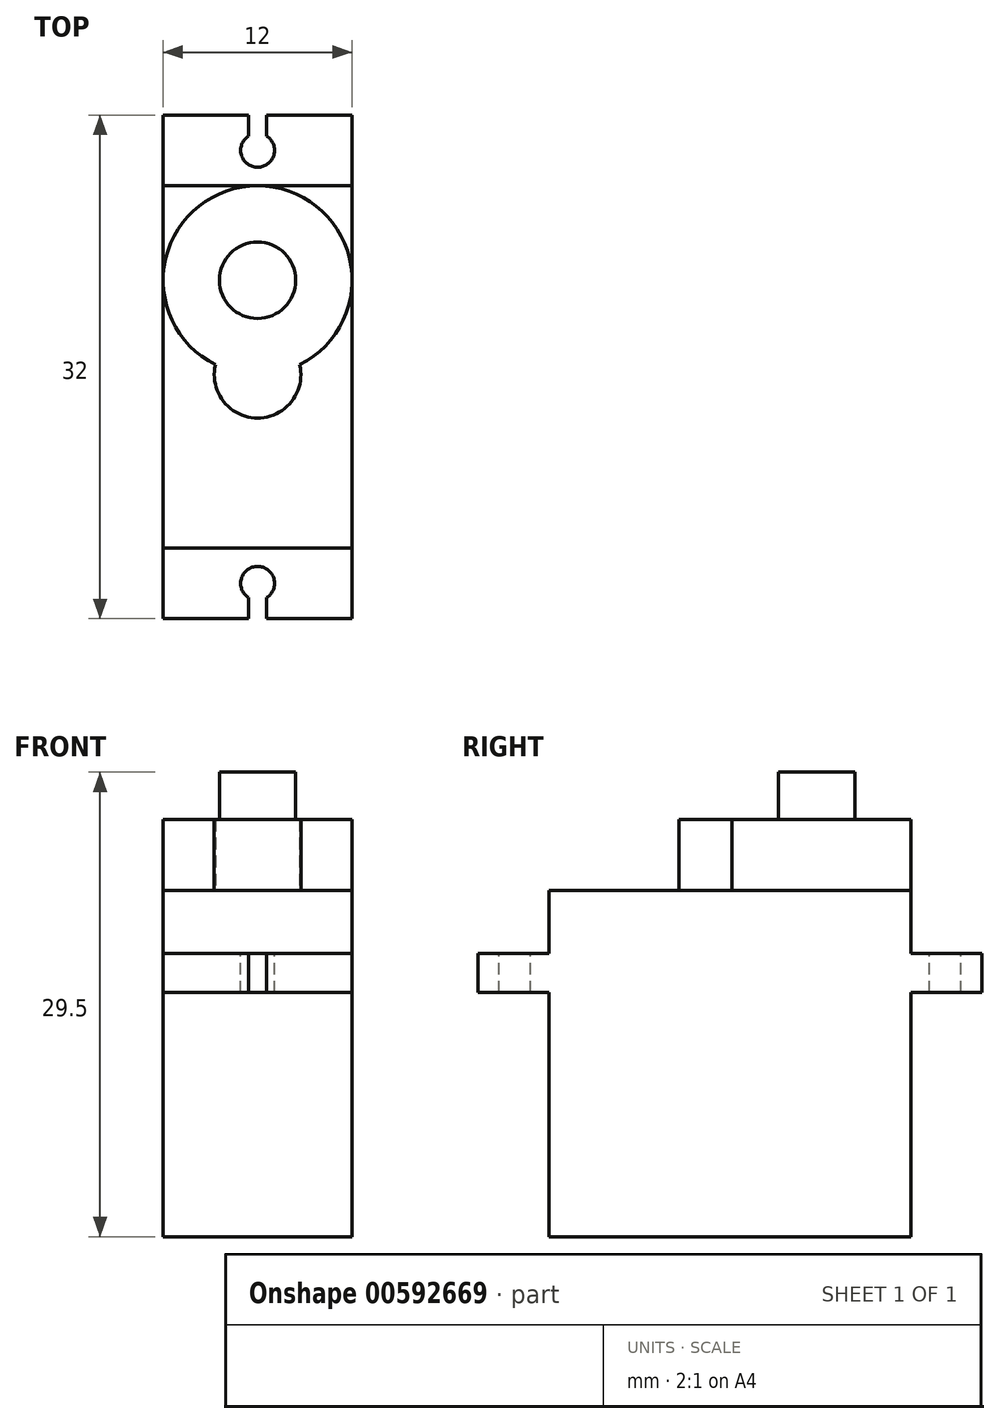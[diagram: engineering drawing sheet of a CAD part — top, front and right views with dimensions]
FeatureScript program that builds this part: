
annotation { "Feature Type Name" : "Feature", "Feature Type Description" : "" }
export const myFeature = defineFeature(function(context is Context, id is Id, definition is map)
    precondition{}
    {
        {
            var Q0;
            Q0=qCreatedBy(makeId("Top.planeOp"),FACE);
            var sketch = newSketch(context, id + "F0", { "sketchPlane" : qUnion([Q0])});
            skLineSegment(sketch, "E0.bottom", {"start": v(0, 0) * mm, "end": v(12, 0) * mm});
            skLineSegment(sketch, "E0.top", {"start": v(0, 23) * mm, "end": v(12, 23) * mm});
            skLineSegment(sketch, "E0.left", {"start": v(0, 0) * mm, "end": v(0, 23) * mm});
            skLineSegment(sketch, "E0.right", {"start": v(12, 0) * mm, "end": v(12, 23) * mm});
            skSolve(sketch);
        }
        {
            var Q0;
            Q0 = qSketchRegion(id + "F0", true);
            extrude(context, id + "F1", {"entities" : qUnion([Q0]), "depth" : 22 * mm, "offsetDistance" : 25 * mm});
        }
        {
            var Q0;
            Q0=qCreatedBy(makeId("Top.planeOp"),FACE);
            cPlane(context, id + "F2", {"entities" : qUnion([Q0]), "cplaneType" : CPlaneType.OFFSET, "offset" : 15.5 * mm, "width" : 150 * mm, "height" : 150 * mm});
        }
        {
            var Q0;
            Q0=qCreatedBy(id+"F2.planeOp",FACE);
            var sketch = newSketch(context, id + "F3", { "sketchPlane" : qUnion([Q0])});
            skLineSegment(sketch, "E1.0", {"start": v(0, 23) * mm, "end": v(12, 23) * mm});
            skPoint(sketch, "E2.0", {"position": v(0, 11.5) * mm});
            skPoint(sketch, "E3.0", {"position": v(12, 11.5) * mm});
            skLineSegment(sketch, "E4", {"start": v(0, 11.5) * mm, "end": v(12, 11.5) * mm, "construction": true});
            skLineSegment(sketch, "E5", {"start": v(0, 23) * mm, "end": v(0, 27.5) * mm});
            skLineSegment(sketch, "E6", {"start": v(0, 27.5) * mm, "end": v(12, 27.5) * mm});
            skLineSegment(sketch, "E7", {"start": v(12, 27.5) * mm, "end": v(12, 23) * mm});
            skLineSegment(sketch, "E8.MirrorCS", {"start": v(0, 0) * mm, "end": v(12, 0) * mm});
            skLineSegment(sketch, "E9.MirrorCS", {"start": v(0, 0) * mm, "end": v(0, -4.5) * mm});
            skLineSegment(sketch, "E10.MirrorCS", {"start": v(0, -4.5) * mm, "end": v(12, -4.5) * mm});
            skLineSegment(sketch, "E11.MirrorCS", {"start": v(12, -4.5) * mm, "end": v(12, 0) * mm});
            skSolve(sketch);
        }
        {
            var Q0;
            Q0 = qSketchRegion(id + "F3", true);
            extrude(context, id + "F4", {"entities" : qUnion([Q0]), "operationType" : NewBodyOperationType.ADD, "depth" : 2.5 * mm, "offsetDistance" : 25 * mm});
        }
        {
            var Q0;
            Q0=makeQuery(id+"F4.opExtrude","CAP_FACE",FACE,{"disambiguationData":[OSD([sQuery(id+"F3.wireOp",EDGE,"E1.0"),sQuery(id+"F3.wireOp",EDGE,"E5"),sQuery(id+"F3.wireOp",EDGE,"E6"),sQuery(id+"F3.wireOp",EDGE,"E7")])],"isStart":false});
            var sketch = newSketch(context, id + "F5", { "sketchPlane" : qUnion([Q0])});
            skCircle(sketch, "E12", {"center": v(6, 25.25) * mm, "radius": 1.07 * mm});
            skPoint(sketch, "E12.centerSnap0", {"position": v(12, 25.25) * mm});
            skPoint(sketch, "E12.centerSnap1", {"position": v(6, 27.5) * mm});
            skLineSegment(sketch, "E13", {"start": v(6, 27.5) * mm, "end": v(6, 25.25) * mm, "construction": true});
            skLineSegment(sketch, "E14", {"start": v(5.42, 27.5) * mm, "end": v(5.42, 26.16) * mm});
            skLineSegment(sketch, "E15", {"start": v(6.58, 27.5) * mm, "end": v(6.58, 26.16) * mm});
            skLineSegment(sketch, "E16", {"start": v(5.42, 27.5) * mm, "end": v(6, 27.5) * mm, "construction": true});
            skLineSegment(sketch, "E17", {"start": v(6, 27.5) * mm, "end": v(6.58, 27.5) * mm, "construction": true});
            skLineSegment(sketch, "E18.0.0", {"start": v(12, 23) * mm, "end": v(0, 23) * mm, "construction": true});
            skLineSegment(sketch, "E18.0.1", {"start": v(0, 23) * mm, "end": v(0, 0) * mm, "construction": true});
            skLineSegment(sketch, "E18.0.2", {"start": v(0, 0) * mm, "end": v(12, 0) * mm, "construction": true});
            skLineSegment(sketch, "E18.0.3", {"start": v(12, 0) * mm, "end": v(12, 23) * mm, "construction": true});
            skLineSegment(sketch, "E19", {"start": v(0, 11.5) * mm, "end": v(12, 11.5) * mm, "construction": true});
            skLineSegment(sketch, "E20.MirrorCS", {"start": v(6.58, -4.5) * mm, "end": v(6.58, -3.16) * mm});
            skCircle(sketch, "E21.MirrorC", {"center": v(6, -2.25) * mm, "radius": 1.07 * mm});
            skLineSegment(sketch, "E22.MirrorCS", {"start": v(6, -4.5) * mm, "end": v(6, -2.25) * mm, "construction": true});
            skPoint(sketch, "E23.MirrorP", {"position": v(6, -4.5) * mm});
            skLineSegment(sketch, "E24.MirrorCS", {"start": v(5.42, -4.5) * mm, "end": v(5.42, -3.16) * mm});
            skLineSegment(sketch, "E25", {"start": v(5.42, 27.5) * mm, "end": v(6.58, 27.5) * mm});
            skLineSegment(sketch, "E26.MirrorCS", {"start": v(5.42, -4.5) * mm, "end": v(6.58, -4.5) * mm});
            skLineSegment(sketch, "E27.MirrorCS", {"start": v(5.42, -4.5) * mm, "end": v(6, -4.5) * mm, "construction": true});
            skLineSegment(sketch, "E28.MirrorCS", {"start": v(6, -4.5) * mm, "end": v(6.58, -4.5) * mm, "construction": true});
            skSolve(sketch);
        }
        {
            var Q0;
            Q0 = qSketchRegion(id + "F5", true);
            extrude(context, id + "F6", {"entities" : qUnion([Q0]), "operationType" : NewBodyOperationType.REMOVE, "endBound" : BoundingType.THROUGH_ALL, "oppositeDirection" : true, "depth" : 25 * mm, "offsetDistance" : 25 * mm});
        }
        {
            var Q0;
            Q0=makeQuery(id+"F1.opExtrude","CAP_FACE",FACE,{"disambiguationData":[OSD([sQuery(id+"F0.wireOp",EDGE,"E0.bottom"),sQuery(id+"F0.wireOp",EDGE,"E0.top"),sQuery(id+"F0.wireOp",EDGE,"E0.left"),sQuery(id+"F0.wireOp",EDGE,"E0.right")])],"isStart":false});
            var sketch = newSketch(context, id + "F7", { "sketchPlane" : qUnion([Q0])});
            skCircle(sketch, "E29", {"center": v(6, 17) * mm, "radius": 6 * mm});
            skPoint(sketch, "E29.centerSnap0", {"position": v(6, 23) * mm});
            skArc(sketch, "E30", {"start": v(3.32, 11.63) * mm, "mid": v(6, 8.25) * mm, "end": v(8.68, 11.63) * mm});
            skSolve(sketch);
        }
        {
            var Q0;
            Q0 = qSketchRegion(id + "F7", true);
            extrude(context, id + "F8", {"entities" : qUnion([Q0]), "operationType" : NewBodyOperationType.ADD, "depth" : 4.5 * mm, "offsetDistance" : 25 * mm});
        }
        {
            var Q0;
            Q0=makeQuery(id+"F8.opExtrude","CAP_FACE",FACE,{"disambiguationData":[OSD([sQuery(id+"F7.wireOp",EDGE,"E29"),sQuery(id+"F7.wireOp",EDGE,"E30")])],"isStart":false});
            var sketch = newSketch(context, id + "F9", { "sketchPlane" : qUnion([Q0])});
            skCircle(sketch, "E31", {"center": v(6, 17) * mm, "radius": 2.43 * mm});
            skSolve(sketch);
        }
        {
            var Q0;
            Q0 = qSketchRegion(id + "F9", true);
            extrude(context, id + "F10", {"entities" : qUnion([Q0]), "operationType" : NewBodyOperationType.ADD, "depth" : 3 * mm, "offsetDistance" : 25 * mm});
        }
    });
